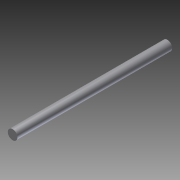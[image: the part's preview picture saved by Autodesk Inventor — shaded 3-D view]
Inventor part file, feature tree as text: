
AUTODESK INVENTOR PART (.ipt)
format: ipt  version: 2012 (Build 160160000, 160)  size: 65,024 bytes
history: native  units: in
note: dims shown in document units (in); Inventor stores cm internally (conversion verified against a paired STEP export)
features: extrude x1, other x1, plane x1, split x1, imported_body x1
ambient origin geometry x8: Origin, YZ Plane, XZ Plane, XY Plane, X Axis, Y Axis, Z Axis, Center Point
feature tree (5):
  extrude  "Extrude1"  [1 undecoded]
  other  "VEX-HINGE-PIN1"
  plane  "Work Plane1"
  split  "Split1"
  imported_body  "Base1"
note: 1 required parameter value undecoded (feature->parameter linkage not recoverable at this tier; creation-order binding heuristic only, values carry confidence <= 0.55)
